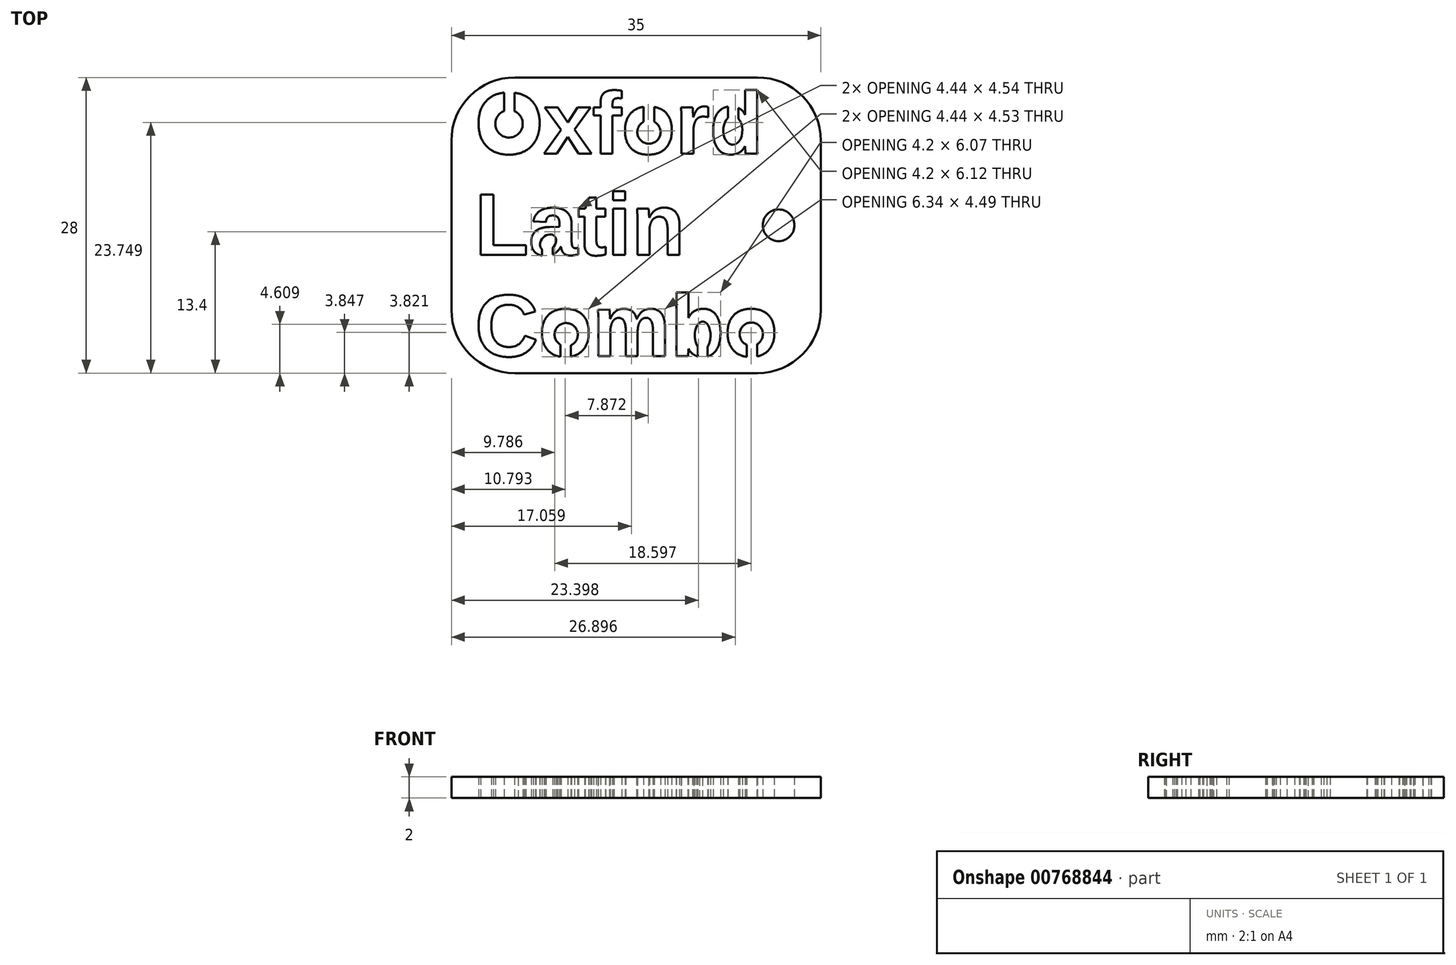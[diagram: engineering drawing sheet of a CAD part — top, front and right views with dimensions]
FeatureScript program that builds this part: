
annotation { "Feature Type Name" : "Feature", "Feature Type Description" : "" }
export const myFeature = defineFeature(function(context is Context, id is Id, definition is map)
    precondition{}
    {
        {
            var Q0;
            Q0=qCreatedBy(makeId("Top.planeOp"),FACE);
            var sketch = newSketch(context, id + "F0", { "sketchPlane" : qUnion([Q0])});
            skText(sketch, "E0", { "text": "Oxford\nLatin\nCombo", "fontName": "Arimo-Bold.ttf"});
            skLineSegment(sketch, "E1.bottom", {"start": v(-31.18, -35.52) * mm, "end": v(3.82, -35.52) * mm});
            skLineSegment(sketch, "E1.top", {"start": v(-31.18, -7.52) * mm, "end": v(3.82, -7.52) * mm});
            skLineSegment(sketch, "E1.left", {"start": v(-31.18, -35.52) * mm, "end": v(-31.18, -7.52) * mm});
            skLineSegment(sketch, "E1.right", {"start": v(3.82, -35.52) * mm, "end": v(3.82, -7.52) * mm});
            skCircle(sketch, "E2", {"center": v(-0.18, -21.52) * mm, "radius": 1.5 * mm});
            skLineSegment(sketch, "E3", {"start": v(3.82, -21.52) * mm, "end": v(-0.18, -21.52) * mm, "construction": true});
            const initialGuessF0  = {"E0": [-0.02895, -0.01475, 1, 0, 0.006]};
            skSetInitialGuess(sketch, initialGuessF0);
            skSolve(sketch);
        }
        {
            var Q0;
            Q0 = qSketchRegion(id + "F0", true);
            extrude(context, id + "F1", {"entities" : qUnion([Q0]), "depth" : 2 * mm, "offsetDistance" : 25 * mm});
        }
        {
            var Q0;
            Q0=qCreatedBy(makeId("Top.planeOp"),FACE);
            var sketch = newSketch(context, id + "F2", { "sketchPlane" : qUnion([Q0])});
            skArc(sketch, "E4", {"start": v(-26.19, -10.7) * mm, "mid": v(-25.75, -13.2) * mm, "end": v(-25.19, -10.72) * mm});
            skLineSegment(sketch, "E5.top", {"start": v(-26.19, -8.44) * mm, "end": v(-25.19, -8.44) * mm});
            skLineSegment(sketch, "E5.left", {"start": v(-26.19, -10.7) * mm, "end": v(-26.19, -8.44) * mm});
            skLineSegment(sketch, "E5.right", {"start": v(-25.19, -10.72) * mm, "end": v(-25.19, -8.44) * mm});
            skArc(sketch, "E6", {"start": v(-12.97, -11.72) * mm, "mid": v(-12.46, -13.8) * mm, "end": v(-11.97, -11.71) * mm});
            skLineSegment(sketch, "E7.top", {"start": v(-12.97, -8.55) * mm, "end": v(-11.97, -8.55) * mm});
            skLineSegment(sketch, "E7.left", {"start": v(-12.97, -11.72) * mm, "end": v(-12.97, -8.55) * mm});
            skLineSegment(sketch, "E7.right", {"start": v(-11.97, -11.71) * mm, "end": v(-11.97, -8.55) * mm});
            skLineSegment(sketch, "E8.top", {"start": v(-4.98, -8.47) * mm, "end": v(-3.98, -8.47) * mm});
            skLineSegment(sketch, "E8.left", {"start": v(-4.98, -11.35) * mm, "end": v(-4.98, -8.47) * mm});
            skLineSegment(sketch, "E8.right", {"start": v(-3.98, -11.43) * mm, "end": v(-3.98, -8.47) * mm});
            skLineSegment(sketch, "E9.top", {"start": v(-21.58, -25.52) * mm, "end": v(-22.58, -25.52) * mm});
            skLineSegment(sketch, "E9.left", {"start": v(-21.58, -23.62) * mm, "end": v(-21.58, -25.52) * mm});
            skLineSegment(sketch, "E9.right", {"start": v(-22.58, -23.78) * mm, "end": v(-22.58, -25.52) * mm});
            skArc(sketch, "E10", {"start": v(-19.86, -32.88) * mm, "mid": v(-20.24, -30.78) * mm, "end": v(-20.86, -32.83) * mm});
            skLineSegment(sketch, "E11.top", {"start": v(-19.86, -34.35) * mm, "end": v(-20.86, -34.35) * mm});
            skLineSegment(sketch, "E11.left", {"start": v(-19.86, -32.88) * mm, "end": v(-19.86, -34.35) * mm});
            skLineSegment(sketch, "E11.right", {"start": v(-20.86, -32.83) * mm, "end": v(-20.86, -34.35) * mm});
            skArc(sketch, "E12", {"start": v(-2.2, -32.78) * mm, "mid": v(-2.83, -30.73) * mm, "end": v(-3.2, -32.84) * mm});
            skLineSegment(sketch, "E13.top", {"start": v(-2.2, -34.94) * mm, "end": v(-3.2, -34.94) * mm});
            skLineSegment(sketch, "E13.left", {"start": v(-2.2, -32.78) * mm, "end": v(-2.2, -34.94) * mm});
            skLineSegment(sketch, "E13.right", {"start": v(-3.2, -32.84) * mm, "end": v(-3.2, -34.94) * mm});
            skLineSegment(sketch, "E14.top", {"start": v(-6.92, -34.75) * mm, "end": v(-7.82, -34.75) * mm});
            skLineSegment(sketch, "E14.left", {"start": v(-6.92, -33.05) * mm, "end": v(-6.92, -34.75) * mm});
            skLineSegment(sketch, "E14.right", {"start": v(-7.82, -33.06) * mm, "end": v(-7.82, -34.75) * mm});
            skLineSegment(sketch, "E15", {"start": v(-20.3, -31.88) * mm, "end": v(-20.3, -34.35) * mm, "construction": true});
            skEllipticalArc(sketch, "E16", {});
            skEllipticalArc(sketch, "E17", {});
            skEllipticalArc(sketch, "E18", {});
            const initialGuessF2  = {"E16": [-0.022020235657691956, -0.023136112838983536, -0.7220790502304184, -0.6918105558747797, 0.0008554956466154424, 0.00065, 1.5504755610571441, 0.11323688577950217], "E17": [-0.007370653136408768, -0.031975821192772466, 0, -1, 0.00135, 0.00075, 0.6466514984830697, 5.642827161855047], "E18": [-0.004519863985478878, -0.01252884604036808, 0, 1, 0.0013642627745866776, 0.0009097794384729241, 0.5300344524324793, 5.6476549042870055]};
            skSetInitialGuess(sketch, initialGuessF2);
            skSolve(sketch);
        }
        {
            var Q0;
            Q0 = qSketchRegion(id + "F2", true);
            extrude(context, id + "F3", {"entities" : qUnion([Q0]), "operationType" : NewBodyOperationType.ADD, "depth" : 2 * mm, "offsetDistance" : 25 * mm});
        }
        {
            var Q0;
            Q0=makeQuery(id+"F1.opExtrude","SWEPT_EDGE",EDGE,{"disambiguationData":[OSD([sQuery(id+"F0.wireOp",EDGE,"E1.bottom"),sQuery(id+"F0.wireOp",EDGE,"E1.left")])]});
            var Q1;
            Q1=makeQuery(id+"F1.opExtrude","SWEPT_EDGE",EDGE,{"disambiguationData":[OSD([sQuery(id+"F0.wireOp",EDGE,"E1.top"),sQuery(id+"F0.wireOp",EDGE,"E1.left")])]});
            var Q2;
            Q2=makeQuery(id+"F1.opExtrude","SWEPT_EDGE",EDGE,{"disambiguationData":[OSD([sQuery(id+"F0.wireOp",EDGE,"E1.bottom"),sQuery(id+"F0.wireOp",EDGE,"E1.right")])]});
            var Q3;
            Q3=makeQuery(id+"F1.opExtrude","SWEPT_EDGE",EDGE,{"disambiguationData":[OSD([sQuery(id+"F0.wireOp",EDGE,"E1.top"),sQuery(id+"F0.wireOp",EDGE,"E1.right")])]});
            fillet(context, id + "F4", {"entities" : qUnion([Q0, Q1, Q2, Q3]), "radius" : 6 * mm, "tangentPropagation" : true, "allowEdgeOverflow" : false});
        }
    });
